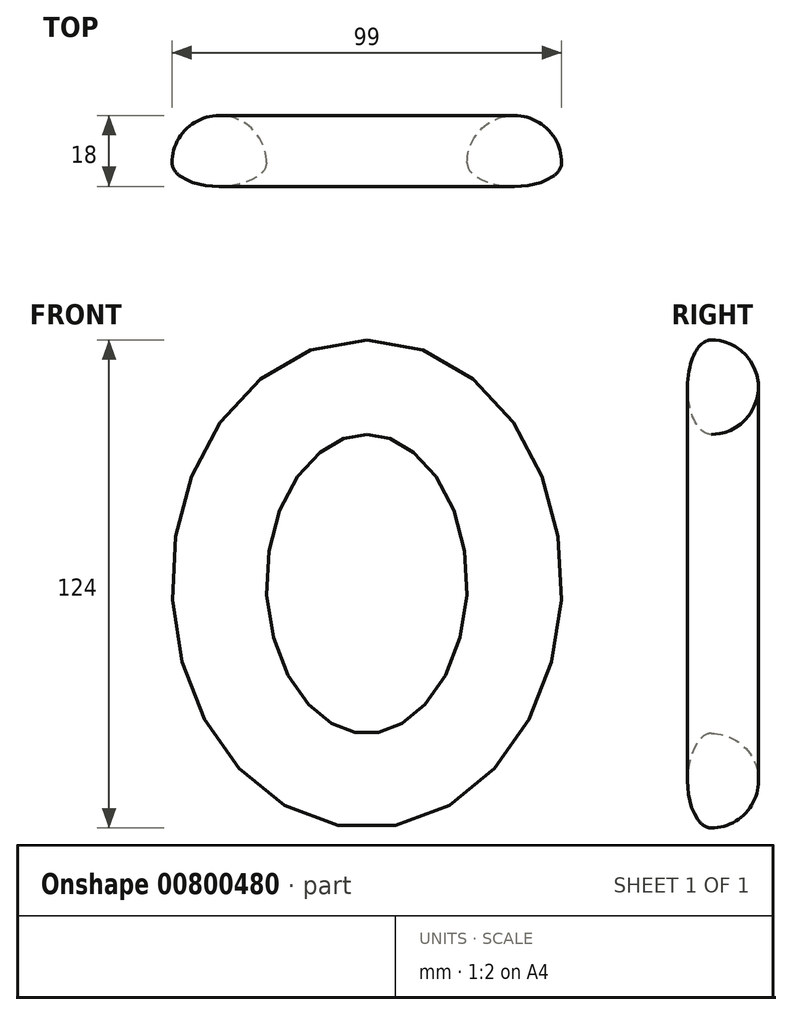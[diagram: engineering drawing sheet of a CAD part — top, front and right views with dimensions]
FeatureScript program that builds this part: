
annotation { "Feature Type Name" : "Feature", "Feature Type Description" : "" }
export const myFeature = defineFeature(function(context is Context, id is Id, definition is map)
    precondition{}
    {
        {
            var Q0;
            Q0=qCreatedBy(makeId("Front.planeOp"),FACE);
            var sketch = newSketch(context, id + "F0", { "sketchPlane" : qUnion([Q0])});
            skEllipse(sketch, "E0", {"center": v(0, 0) * mm, "majorRadius": 50 * mm, "minorRadius": 37.5 * mm, "majorAxis": v(0, 1)});
            skSolve(sketch);
        }
        {
            var Q0;
            Q0=qCreatedBy(makeId("Right.planeOp"),FACE);
            var sketch = newSketch(context, id + "F1", { "sketchPlane" : qUnion([Q0])});
            skLineSegment(sketch, "E1.0", {"start": v(0, -50) * mm, "end": v(0, 50) * mm, "construction": true});
            skPoint(sketch, "E2", {"position": v(0, 62) * mm});
            skPoint(sketch, "E3", {"position": v(0, 38) * mm});
            skEllipticalArc(sketch, "E4", {});
            skEllipticalArc(sketch, "E5", {});
            const initialGuessF1  = {"E4": [0, 0.05, 7.232008480961838e-08, 1, 0.012, 0.006, 0, 3.141592653589793], "E5": [0, 0.05, 0, 1, 0.012, 0.012, 3.141592653589793, 0]};
            skSetInitialGuess(sketch, initialGuessF1);
            skSolve(sketch);
        }
        {
            var Q0;
            Q0 = qSketchRegion(id + "F1", true);
            var Q1;
            Q1 = qConstructionFilter(qBodyType(qCreatedBy(id + "F0" ,EDGE), BodyType.WIRE), ConstructionObject.NO);
            sweep(context, id + "F2", {"profiles" : qUnion([Q0]), "path" : qUnion([Q1])});
        }
    });
